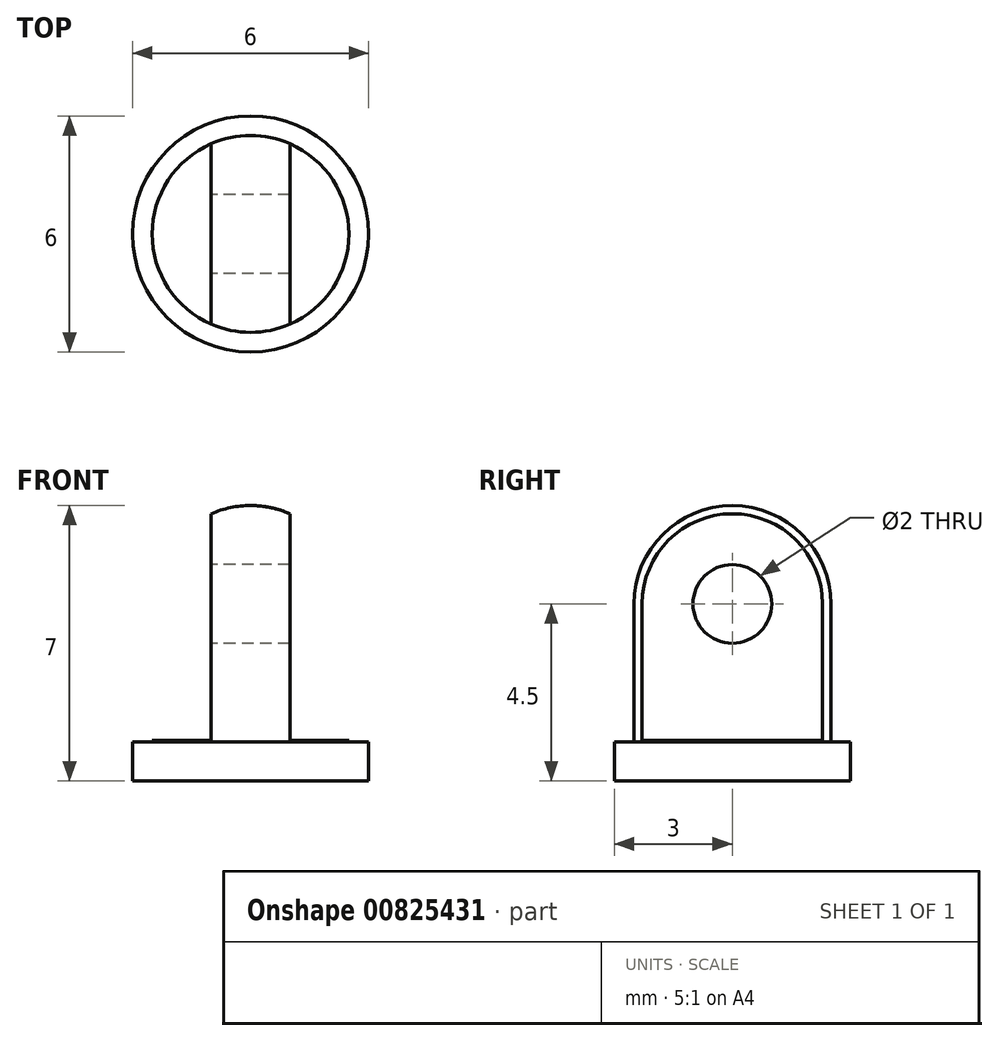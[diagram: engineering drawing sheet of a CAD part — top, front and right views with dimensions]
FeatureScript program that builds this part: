
annotation { "Feature Type Name" : "Feature", "Feature Type Description" : "" }
export const myFeature = defineFeature(function(context is Context, id is Id, definition is map)
    precondition{}
    {
        {
            var Q0;
            Q0=qCreatedBy(makeId("Top.planeOp"),FACE);
            var sketch = newSketch(context, id + "F0", { "sketchPlane" : qUnion([Q0])});
            skCircle(sketch, "E0", {"center": v(0, 0) * mm, "radius": 3 * mm});
            skSolve(sketch);
        }
        {
            var Q0;
            Q0=makeQuery(id+"F0.imprint","IMPRINT",FACE,{"disambiguationData":[TD([[makeQuery(id+"F0.imprint","IMPRINT",EDGE,{"derivedFrom":sQuery(id+"F0.wireOp",EDGE,"E0")}),1.0]])]});
            var Q1;
            Q1=sQuery(id+"F0.wireOp",EDGE,"E0");
            extrude(context, id + "F1", {"entities" : qUnion([Q0]), "surfaceEntities" : qUnion([Q1]), "depth" : 1 * mm, "offsetDistance" : 25 * mm});
        }
        {
            var Q0;
            Q0=makeQuery(id+"F1.opExtrude","CAP_FACE",FACE,{"disambiguationData":[OSD([sQuery(id+"F0.wireOp",EDGE,"E0")])],"isStart":false});
            var sketch = newSketch(context, id + "F2", { "sketchPlane" : qUnion([Q0])});
            skCircle(sketch, "E1", {"center": v(0, 0) * mm, "radius": 2.5 * mm});
            skSolve(sketch);
        }
        {
            var Q0;
            Q0=makeQuery(id+"F2.imprint","IMPRINT",FACE,{"disambiguationData":[TD([[makeQuery(id+"F2.imprint","IMPRINT",EDGE,{"derivedFrom":sQuery(id+"F2.wireOp",EDGE,"E1")}),1.0]])]});
            var Q1;
            Q1=sQuery(id+"F2.wireOp",EDGE,"E1");
            extrude(context, id + "F3", {"entities" : qUnion([Q0]), "surfaceEntities" : qUnion([Q1]), "depth" : 6 * mm, "offsetDistance" : 25 * mm});
        }
        {
            var Q0;
            Q0=makeQuery(id+"F3.opExtrude","CAP_EDGE",EDGE,{"disambiguationData":[OSD([sQuery(id+"F2.wireOp",EDGE,"E1")])],"isStart":false});
            fillet(context, id + "F4", {"entities" : qUnion([Q0]), "radius" : 2.5 * mm, "tangentPropagation" : true, "allowEdgeOverflow" : false});
        }
        {
            var Q0;
            Q0=qCreatedBy(makeId("Front.planeOp"),FACE);
            var sketch = newSketch(context, id + "F5", { "sketchPlane" : qUnion([Q0])});
            skLineSegment(sketch, "E2", {"start": v(0, 0) * mm, "end": v(0, 10.63) * mm, "construction": true});
            skLineSegment(sketch, "E3", {"start": v(0, 0) * mm, "end": v(1, 0) * mm, "construction": true});
            skLineSegment(sketch, "E4", {"start": v(1, 0) * mm, "end": v(1, 10.77) * mm, "construction": true});
            skLineSegment(sketch, "E5", {"start": v(0, 0) * mm, "end": v(-1, 0) * mm, "construction": true});
            skLineSegment(sketch, "E6", {"start": v(-1, 0) * mm, "end": v(-1, 10.87) * mm, "construction": true});
            skLineSegment(sketch, "E7", {"start": v(-3.06, 1.04) * mm, "end": v(-1, 1.04) * mm, "construction": true});
            skLineSegment(sketch, "E8", {"start": v(-1, 10.63) * mm, "end": v(-3, 10.63) * mm});
            skLineSegment(sketch, "E9", {"start": v(-3, 10.63) * mm, "end": v(-3, 1.04) * mm});
            skLineSegment(sketch, "E10", {"start": v(-3, 1.04) * mm, "end": v(-1, 1.04) * mm});
            skLineSegment(sketch, "E11", {"start": v(-1, 1.04) * mm, "end": v(-1, 10.87) * mm});
            skLineSegment(sketch, "E12", {"start": v(1, 10.63) * mm, "end": v(2.77, 10.63) * mm});
            skLineSegment(sketch, "E13", {"start": v(2.77, 10.63) * mm, "end": v(2.77, 1.04) * mm});
            skLineSegment(sketch, "E14", {"start": v(2.77, 1.04) * mm, "end": v(1, 1.04) * mm});
            skLineSegment(sketch, "E15", {"start": v(1, 1.04) * mm, "end": v(1, 10.77) * mm});
            skLineSegment(sketch, "E16.trimOffspring", {"start": v(1, 1.04) * mm, "end": v(2.98, 1.04) * mm, "construction": true});
            skSolve(sketch);
        }
        {
            var Q0;
            Q0 = qSketchRegion(id + "F5", true);
            extrude(context, id + "F6", {"entities" : qUnion([Q0]), "operationType" : NewBodyOperationType.REMOVE, "endBound" : BoundingType.SYMMETRIC, "oppositeDirection" : true, "depth" : 25 * mm, "offsetDistance" : 25 * mm});
        }
        {
            var Q0;
            Q0=makeQuery(id+"F6.boolean.opBoolean","COPY",FACE,{"derivedFrom":makeQuery(id+"F6.opExtrude","SWEPT_FACE",FACE,{"disambiguationData":[OSD([sQuery(id+"F5.wireOp",EDGE,"E11")])]})});
            var sketch = newSketch(context, id + "F7", { "sketchPlane" : qUnion([Q0])});
            skLineSegment(sketch, "E17", {"start": v(-2.3, 4.5) * mm, "end": v(2.3, 4.5) * mm, "construction": true});
            skLineSegment(sketch, "E18", {"start": v(0, 8.19) * mm, "end": v(0, 1.04) * mm, "construction": true});
            skPoint(sketch, "E18.startSnap0", {"position": v(0, 6.8) * mm});
            skCircle(sketch, "E19", {"center": v(0, 4.5) * mm, "radius": 1 * mm});
            skSolve(sketch);
        }
        {
            var Q0;
            Q0=makeQuery(id+"F7.imprint","IMPRINT",FACE,{"disambiguationData":[TD([[makeQuery(id+"F7.imprint","IMPRINT",EDGE,{"derivedFrom":sQuery(id+"F7.wireOp",EDGE,"E19")}),1.0]])]});
            var Q1;
            Q1=sQuery(id+"F7.wireOp",EDGE,"E19");
            extrude(context, id + "F8", {"entities" : qUnion([Q0]), "operationType" : NewBodyOperationType.REMOVE, "surfaceEntities" : qUnion([Q1]), "endBound" : BoundingType.THROUGH_ALL, "oppositeDirection" : true, "depth" : 25 * mm, "offsetDistance" : 25 * mm});
        }
    });
